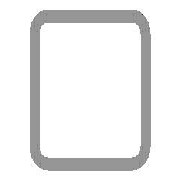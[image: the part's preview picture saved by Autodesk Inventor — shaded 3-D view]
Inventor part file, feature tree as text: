
AUTODESK INVENTOR PART (.ipt)
format: ipt  version: 2016 (Build 200138000, 138)  size: 135,680 bytes
history: native  units: mm (DEFAULTED — no unit token found)
features: other x4, plane x3, sketch x3, split x2
ambient origin geometry x8: Origin, YZ Plane, XZ Plane, XY Plane, X Axis, Y Axis, Z Axis, Center Point
bodies: Solid1 (feature_tree), Body (feature_tree)
feature tree (12):
  parser-record x1  (decoder bookkeeping rows leaked as tree rows — omitted from the tree; the rows remain in map.json)
  other  "Driven Length"
  other  "Start plane"
  other  "End plane"
  plane  "Work Plane4"
  split  "Split1"
  plane  "Work Plane5"
  split  "Split2"
  sketch  "Sketch"  dims[d7=4.0mm d9=25.0mm d11=25.0mm d12=2.0mm d13=25.0mm d14=285.0mm d15=12.5mm d16=12.5mm d17=90.0deg d18=260.0mm]
  sketch  "Sketch3"  dims[d3=260.0mm]
  plane  "Work Plane3"
  sketch  "Sketch4"  dims[d4=0.0mm]
